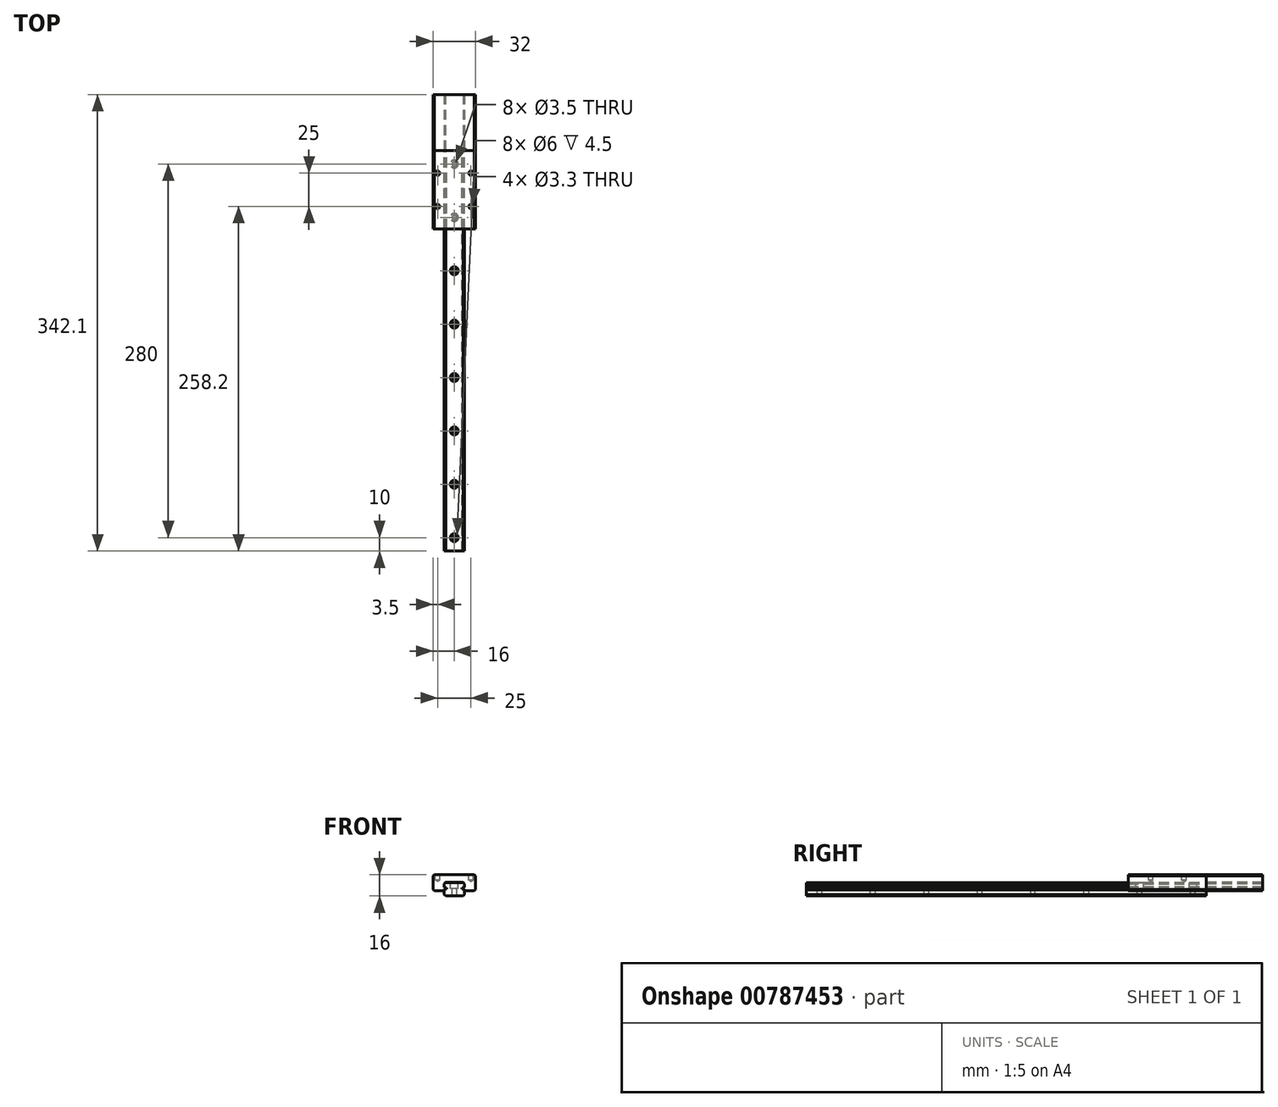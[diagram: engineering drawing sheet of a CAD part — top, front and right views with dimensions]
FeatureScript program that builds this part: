
annotation { "Feature Type Name" : "Feature", "Feature Type Description" : "" }
export const myFeature = defineFeature(function(context is Context, id is Id, definition is map)
    precondition{}
    {
        {
            var Q0;
            Q0=qCreatedBy(makeId("Front.planeOp"),FACE);
            var sketch = newSketch(context, id + "F0", { "sketchPlane" : qUnion([Q0])});
            skLineSegment(sketch, "E0.bottom", {"start": v(6.5, -5) * mm, "end": v(-6.5, -5) * mm});
            skLineSegment(sketch, "E0.top", {"start": v(6.5, 5) * mm, "end": v(-6.5, 5) * mm});
            skLineSegment(sketch, "E0.left", {"start": v(7.5, -4) * mm, "end": v(7.5, -0.41) * mm});
            skLineSegment(sketch, "E0.right", {"start": v(-7.5, -4) * mm, "end": v(-7.5, -0.41) * mm});
            skPoint(sketch, "E0.middle", {"position": v(0, 0) * mm});
            skLineSegment(sketch, "E1", {"start": v(0, 12.36) * mm, "end": v(0, -9.73) * mm, "construction": true});
            skLineSegment(sketch, "E2", {"start": v(-7.5, 2) * mm, "end": v(-6.8, 1.3) * mm});
            skLineSegment(sketch, "E3", {"start": v(-6.8, 1.3) * mm, "end": v(-5.8, 1.3) * mm});
            skLineSegment(sketch, "E4", {"start": v(-5.8, 1.3) * mm, "end": v(-5.8, 0.3) * mm});
            skLineSegment(sketch, "E5", {"start": v(-5.8, 0.3) * mm, "end": v(-6.8, 0.3) * mm});
            skLineSegment(sketch, "E6", {"start": v(-6.8, 0.3) * mm, "end": v(-7.5, -0.41) * mm});
            skLineSegment(sketch, "E7.MirrorCS", {"start": v(5.8, 0.3) * mm, "end": v(6.8, 0.3) * mm});
            skLineSegment(sketch, "E8.MirrorCS", {"start": v(6.8, 0.3) * mm, "end": v(7.5, -0.41) * mm});
            skLineSegment(sketch, "E9.MirrorCS", {"start": v(5.8, 1.3) * mm, "end": v(5.8, 0.3) * mm});
            skLineSegment(sketch, "E10.MirrorCS", {"start": v(7.5, 2) * mm, "end": v(6.8, 1.3) * mm});
            skLineSegment(sketch, "E11.MirrorCS", {"start": v(6.8, 1.3) * mm, "end": v(5.8, 1.3) * mm});
            skLineSegment(sketch, "E12.trimOffspring", {"start": v(-7.5, 2) * mm, "end": v(-7.5, 4) * mm});
            skLineSegment(sketch, "E13.trimOffspring", {"start": v(7.5, 2) * mm, "end": v(7.5, 4) * mm});
            skLineSegment(sketch, "E14", {"start": v(-7.5, 4) * mm, "end": v(-6.5, 5) * mm});
            skLineSegment(sketch, "E15.MirrorCS", {"start": v(7.5, 4) * mm, "end": v(6.5, 5) * mm});
            skLineSegment(sketch, "E16.MirrorCS", {"start": v(-7.5, -4) * mm, "end": v(-6.5, -5) * mm});
            skLineSegment(sketch, "E17.MirrorCS", {"start": v(7.5, -4) * mm, "end": v(6.5, -5) * mm});
            skPoint(sketch, "E18.orphan", {"position": v(-7.5, 5) * mm});
            skPoint(sketch, "E19.orphan", {"position": v(7.5, 5) * mm});
            skPoint(sketch, "E20.orphan", {"position": v(7.5, -5) * mm});
            skPoint(sketch, "E21.orphan", {"position": v(-7.5, -5) * mm});
            skSolve(sketch);
        }
        {
            var Q0;
            Q0=makeQuery(id+"F0.imprint","IMPRINT",FACE,{"disambiguationData":[TD([[makeQuery(id+"F0.imprint","IMPRINT",EDGE,{"derivedFrom":sQuery(id+"F0.wireOp",EDGE,"E0.bottom")}),-1.0]])]});
            extrude(context, id + "F1", {"entities" : qUnion([Q0]), "depth" : 300 * mm, "offsetDistance" : 25 * mm});
        }
        {
            var Q0;
            Q0=makeQuery(id+"F1.opExtrude","SWEPT_FACE",FACE,{"disambiguationData":[OSD([sQuery(id+"F0.wireOp",EDGE,"E0.top")])]});
            var sketch = newSketch(context, id + "F2", { "sketchPlane" : qUnion([Q0])});
            skLineSegment(sketch, "E22", {"start": v(0, 4.61) * mm, "end": v(0, -375.08) * mm, "construction": true});
            skCircle(sketch, "E23", {"center": v(0, -10) * mm, "radius": 1.75 * mm});
            skCircle(sketch, "E24.1.0.0", {"center": v(0, -50) * mm, "radius": 1.75 * mm});
            skCircle(sketch, "E24.2.0.0", {"center": v(0, -90) * mm, "radius": 1.75 * mm});
            skCircle(sketch, "E24.3.0.0", {"center": v(0, -130) * mm, "radius": 1.75 * mm});
            skCircle(sketch, "E24.4.0.0", {"center": v(0, -170) * mm, "radius": 1.75 * mm});
            skCircle(sketch, "E24.5.0.0", {"center": v(0, -210) * mm, "radius": 1.75 * mm});
            skCircle(sketch, "E24.6.0.0", {"center": v(0, -250) * mm, "radius": 1.75 * mm});
            skCircle(sketch, "E24.7.0.0", {"center": v(0, -290) * mm, "radius": 1.75 * mm});
            skCircle(sketch, "E24.8.0.0", {"center": v(0, -330) * mm, "radius": 1.75 * mm});
            skLineSegment(sketch, "E24.direction1", {"start": v(0, -10) * mm, "end": v(0, -50) * mm, "construction": true});
            skSolve(sketch);
        }
        {
            var Q0;
            Q0=qSketchRegion(id+"F2",true);
            extrude(context, id + "F3", {"entities" : qUnion([Q0]), "operationType" : NewBodyOperationType.REMOVE, "endBound" : BoundingType.THROUGH_ALL, "oppositeDirection" : true, "depth" : 25 * mm, "offsetDistance" : 25 * mm});
        }
        {
            var Q0;
            Q0=makeQuery(id+"F1.opExtrude","SWEPT_FACE",FACE,{"disambiguationData":[OSD([sQuery(id+"F0.wireOp",EDGE,"E0.top")])]});
            var sketch = newSketch(context, id + "F4", { "sketchPlane" : qUnion([Q0])});
            skLineSegment(sketch, "E25", {"start": v(0, 167.82) * mm, "end": v(0, -211.88) * mm, "construction": true});
            skCircle(sketch, "E26", {"center": v(0, -10) * mm, "radius": 3 * mm});
            skCircle(sketch, "E27.1.0.0", {"center": v(0, -50) * mm, "radius": 3 * mm});
            skCircle(sketch, "E27.2.0.0", {"center": v(0, -90) * mm, "radius": 3 * mm});
            skCircle(sketch, "E27.3.0.0", {"center": v(0, -130) * mm, "radius": 3 * mm});
            skCircle(sketch, "E27.4.0.0", {"center": v(0, -170) * mm, "radius": 3 * mm});
            skCircle(sketch, "E27.5.0.0", {"center": v(0, -210) * mm, "radius": 3 * mm});
            skCircle(sketch, "E27.6.0.0", {"center": v(0, -250) * mm, "radius": 3 * mm});
            skCircle(sketch, "E27.7.0.0", {"center": v(0, -290) * mm, "radius": 3 * mm});
            skCircle(sketch, "E27.8.0.0", {"center": v(0, -330) * mm, "radius": 3 * mm});
            skLineSegment(sketch, "E27.direction1", {"start": v(0, -10) * mm, "end": v(0, -50) * mm, "construction": true});
            skSolve(sketch);
        }
        {
            var Q0;
            Q0=qSketchRegion(id+"F4",true);
            extrude(context, id + "F5", {"entities" : qUnion([Q0]), "operationType" : NewBodyOperationType.REMOVE, "oppositeDirection" : true, "depth" : 4.5 * mm, "offsetDistance" : 25 * mm});
        }
        {
            var Q0;
            Q0=qCreatedBy(makeId("Front.planeOp"),FACE);
            var sketch = newSketch(context, id + "F6", { "sketchPlane" : qUnion([Q0])});
            skLineSegment(sketch, "E28", {"start": v(-7.65, -1) * mm, "end": v(-15, -1) * mm});
            skLineSegment(sketch, "E29", {"start": v(-16, 0) * mm, "end": v(-16, 10) * mm});
            skLineSegment(sketch, "E30", {"start": v(-15, 11) * mm, "end": v(0, 11) * mm});
            skLineSegment(sketch, "E31", {"start": v(-7.65, -1) * mm, "end": v(-7.65, -0.35) * mm});
            skLineSegment(sketch, "E32", {"start": v(-7.65, -0.35) * mm, "end": v(-6.8, 0.5) * mm});
            skLineSegment(sketch, "E33", {"start": v(-6.8, 0.5) * mm, "end": v(-6.8, 1.08) * mm});
            skLineSegment(sketch, "E34", {"start": v(-6.8, 1.08) * mm, "end": v(-7.65, 1.94) * mm});
            skLineSegment(sketch, "E35", {"start": v(-7.65, 1.94) * mm, "end": v(-7.65, 4.06) * mm});
            skLineSegment(sketch, "E36", {"start": v(-7.65, 4.06) * mm, "end": v(-6.56, 5.15) * mm});
            skLineSegment(sketch, "E37", {"start": v(-6.56, 5.15) * mm, "end": v(0, 5.15) * mm});
            skLineSegment(sketch, "E38", {"start": v(-16, 10) * mm, "end": v(-15, 11) * mm});
            skLineSegment(sketch, "E39", {"start": v(-15, -1) * mm, "end": v(-16, 0) * mm});
            skPoint(sketch, "E40.orphan", {"position": v(-16, -1) * mm});
            skPoint(sketch, "E41.orphan", {"position": v(-16, 11) * mm});
            skLineSegment(sketch, "E42.MirrorCS", {"start": v(15, 11) * mm, "end": v(0, 11) * mm});
            skLineSegment(sketch, "E43.MirrorCS", {"start": v(16, 10) * mm, "end": v(15, 11) * mm});
            skLineSegment(sketch, "E44.MirrorCS", {"start": v(16, 0) * mm, "end": v(16, 10) * mm});
            skLineSegment(sketch, "E45.MirrorCS", {"start": v(15, -1) * mm, "end": v(16, 0) * mm});
            skLineSegment(sketch, "E46.MirrorCS", {"start": v(7.65, -1) * mm, "end": v(15, -1) * mm});
            skLineSegment(sketch, "E47.MirrorCS", {"start": v(7.65, -1) * mm, "end": v(7.65, -0.35) * mm});
            skLineSegment(sketch, "E48.MirrorCS", {"start": v(7.65, -0.35) * mm, "end": v(6.8, 0.5) * mm});
            skLineSegment(sketch, "E49.MirrorCS", {"start": v(6.8, 0.5) * mm, "end": v(6.8, 1.08) * mm});
            skLineSegment(sketch, "E50.MirrorCS", {"start": v(6.8, 1.08) * mm, "end": v(7.65, 1.94) * mm});
            skLineSegment(sketch, "E51.MirrorCS", {"start": v(7.65, 1.94) * mm, "end": v(7.65, 4.06) * mm});
            skLineSegment(sketch, "E52.MirrorCS", {"start": v(7.65, 4.06) * mm, "end": v(6.56, 5.15) * mm});
            skLineSegment(sketch, "E53.MirrorCS", {"start": v(6.56, 5.15) * mm, "end": v(0, 5.15) * mm});
            skSolve(sketch);
        }
        {
            var Q0;
            Q0=qSketchRegion(id+"F6",true);
            extrude(context, id + "F7", {"entities" : qUnion([Q0]), "depth" : 58.6 * mm, "offsetDistance" : 25 * mm});
        }
        {
            var Q0;
            Q0=qSketchRegion(id+"F6",true);
            extrude(context, id + "F8", {"entities" : qUnion([Q0]), "oppositeDirection" : true, "depth" : 42.1 * mm, "offsetDistance" : 25 * mm});
        }
        {
            var Q0;
            Q0=makeQuery(id+"F7.opExtrude","SWEPT_FACE",FACE,{"disambiguationData":[OSD([sQuery(id+"F6.wireOp",EDGE,"E30"),sQuery(id+"F6.wireOp",EDGE,"E42.MirrorCS")])]});
            var sketch = newSketch(context, id + "F9", { "sketchPlane" : qUnion([Q0])});
            skLineSegment(sketch, "E54", {"start": v(-15, 0) * mm, "end": v(15, -58.6) * mm, "construction": true});
            skLineSegment(sketch, "E55", {"start": v(15, 0) * mm, "end": v(-15, -58.6) * mm, "construction": true});
            skLineSegment(sketch, "E56", {"start": v(-37.81, -29.3) * mm, "end": v(32.35, -29.3) * mm, "construction": true});
            skPoint(sketch, "E56.startSnap0", {"position": v(0, -29.3) * mm});
            skLineSegment(sketch, "E57", {"start": v(0, 0) * mm, "end": v(0, -61.52) * mm, "construction": true});
            skCircle(sketch, "E58", {"center": v(-12.5, -16.8) * mm, "radius": 1.5 * mm});
            skCircle(sketch, "E59.MirrorC", {"center": v(12.5, -16.8) * mm, "radius": 1.5 * mm});
            skCircle(sketch, "E60.MirrorC", {"center": v(-12.5, -41.8) * mm, "radius": 1.5 * mm});
            skCircle(sketch, "E61.MirrorC", {"center": v(12.5, -41.8) * mm, "radius": 1.5 * mm});
            skSolve(sketch);
        }
        {
            var Q0;
            Q0=sQuery(id+"F9.wireOp",VERTEX,"E58.center");
            var Q1;
            Q1=sQuery(id+"F9.wireOp",VERTEX,"E59.MirrorC.center");
            var Q2;
            Q2=sQuery(id+"F9.wireOp",VERTEX,"E60.MirrorC.center");
            var Q3;
            Q3=sQuery(id+"F9.wireOp",VERTEX,"E61.MirrorC.center");
            var Q4;
            Q4=makeQuery(id+"F7.opExtrude","SWEPT_BODY",BODY,{"disambiguationData":[OSD([sQuery(id+"F6.wireOp",EDGE,"E28"),sQuery(id+"F6.wireOp",EDGE,"E29"),sQuery(id+"F6.wireOp",EDGE,"E30"),sQuery(id+"F6.wireOp",EDGE,"E31"),sQuery(id+"F6.wireOp",EDGE,"E32"),sQuery(id+"F6.wireOp",EDGE,"E33"),sQuery(id+"F6.wireOp",EDGE,"E34"),sQuery(id+"F6.wireOp",EDGE,"E35"),sQuery(id+"F6.wireOp",EDGE,"E36"),sQuery(id+"F6.wireOp",EDGE,"E37"),sQuery(id+"F6.wireOp",EDGE,"E38"),sQuery(id+"F6.wireOp",EDGE,"E39"),sQuery(id+"F6.wireOp",EDGE,"E42.MirrorCS"),sQuery(id+"F6.wireOp",EDGE,"E43.MirrorCS"),sQuery(id+"F6.wireOp",EDGE,"E44.MirrorCS"),sQuery(id+"F6.wireOp",EDGE,"E45.MirrorCS"),sQuery(id+"F6.wireOp",EDGE,"E46.MirrorCS"),sQuery(id+"F6.wireOp",EDGE,"E47.MirrorCS"),sQuery(id+"F6.wireOp",EDGE,"E48.MirrorCS"),sQuery(id+"F6.wireOp",EDGE,"E49.MirrorCS"),sQuery(id+"F6.wireOp",EDGE,"E50.MirrorCS"),sQuery(id+"F6.wireOp",EDGE,"E51.MirrorCS"),sQuery(id+"F6.wireOp",EDGE,"E52.MirrorCS"),sQuery(id+"F6.wireOp",EDGE,"E53.MirrorCS")])]});
            hole(context, id + "F10", {"style" : HoleStyle.SIMPLE, "endStyle" : HoleEndStyle.BLIND, "standardTappedOrClearance" : lookupTablePath({ "standard" : "ISO", "fit" : "Normal", "size" : "M3", "type" : "Clearance" }), "standardBlindInLast" : lookupTablePath({ "fit" : "Standard", "standard" : "ISO", "size" : "M3", "type" : "Clearance" }), "holeDiameter" : 3.3 * mm, "majorDiameter" : 5 * mm, "holeDepth" : 4 * mm, "isTappedThrough" : true, "tappedDepth" : 12 * mm, "tapClearance" : 3, "startFromSketch" : true, "locations" : qUnion([Q0, Q1, Q2, Q3]), "scope" : qUnion([Q4])});
        }
    });
